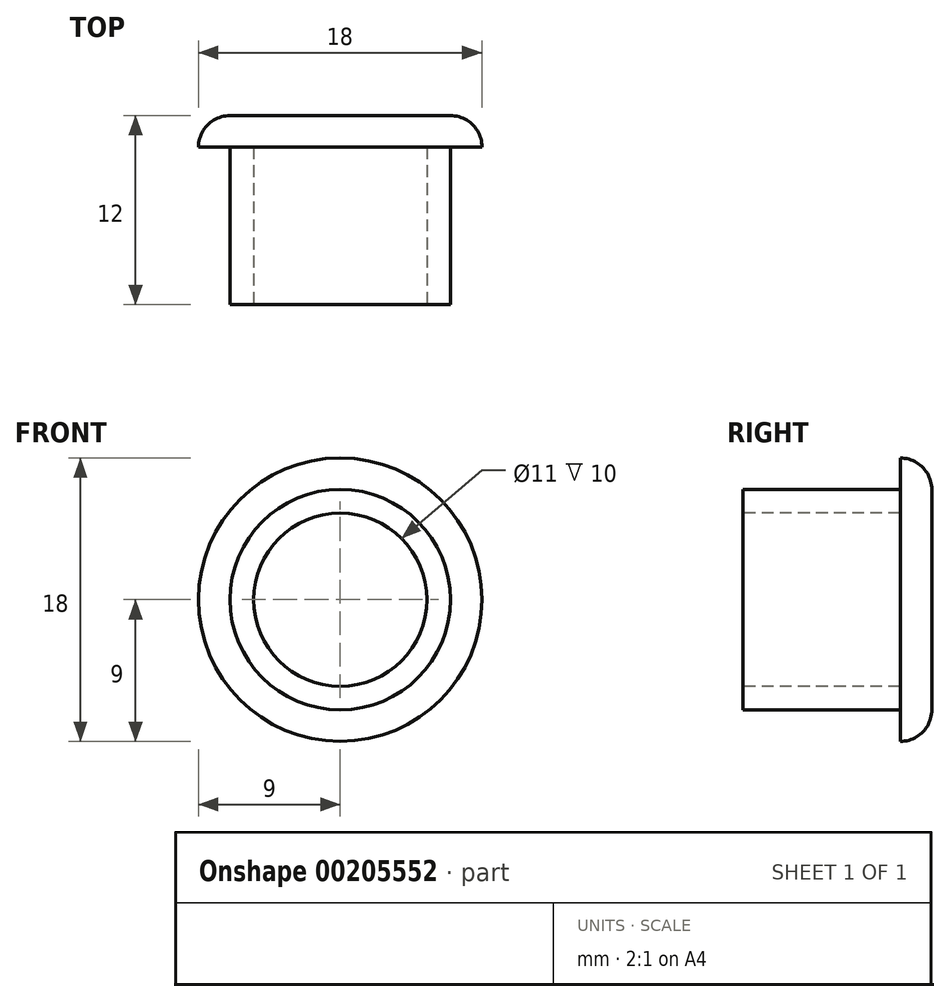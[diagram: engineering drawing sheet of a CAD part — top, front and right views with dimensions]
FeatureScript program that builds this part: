
annotation { "Feature Type Name" : "Feature", "Feature Type Description" : "" }
export const myFeature = defineFeature(function(context is Context, id is Id, definition is map)
    precondition{}
    {
        {
            var Q0;
            Q0=qCreatedBy(makeId("Front.planeOp"),FACE);
            var sketch = newSketch(context, id + "F0", { "sketchPlane" : qUnion([Q0])});
            skCircle(sketch, "E0", {"center": v(0, 0) * mm, "radius": 9 * mm});
            skSolve(sketch);
        }
        {
            var Q0;
            Q0=qSketchRegion(id+"F0",true);
            extrude(context, id + "F1", {"entities" : qUnion([Q0]), "depth" : 12 * mm});
        }
        {
            var Q0;
            Q0=makeQuery(id+"F1.opExtrude","CAP_FACE",FACE,{"disambiguationData":[OSD([sQuery(id+"F0.wireOp",EDGE,"E0")])],"isStart":false});
            var sketch = newSketch(context, id + "F2", { "sketchPlane" : qUnion([Q0])});
            skCircle(sketch, "E1", {"center": v(0, 0) * mm, "radius": 7 * mm});
            skSolve(sketch);
        }
        {
            var Q0;
            Q0=makeQuery(id+"F2.imprint","IMPRINT",FACE,{"disambiguationData":[TD([[makeQuery(id+"F2.imprint","IMPRINT",EDGE,{"derivedFrom":sQuery(id+"F2.wireOp",EDGE,"E1")}),-1.0]])]});
            extrude(context, id + "F3", {"entities" : qUnion([Q0]), "operationType" : NewBodyOperationType.REMOVE, "oppositeDirection" : true, "depth" : 10 * mm});
        }
        {
            var Q0;
            Q0=makeQuery(id+"F1.opExtrude","CAP_FACE",FACE,{"disambiguationData":[OSD([sQuery(id+"F0.wireOp",EDGE,"E0")])],"isStart":false});
            var sketch = newSketch(context, id + "F4", { "sketchPlane" : qUnion([Q0])});
            skCircle(sketch, "E2", {"center": v(0, 0) * mm, "radius": 5.5 * mm});
            skSolve(sketch);
        }
        {
            var Q0;
            Q0=qSketchRegion(id+"F4",true);
            extrude(context, id + "F5", {"entities" : qUnion([Q0]), "operationType" : NewBodyOperationType.REMOVE, "oppositeDirection" : true, "depth" : 10 * mm});
        }
        {
            var Q0;
            Q0=makeQuery(id+"F1.opExtrude","CAP_FACE",FACE,{"disambiguationData":[OSD([sQuery(id+"F0.wireOp",EDGE,"E0")])],"isStart":true});
            fillet(context, id + "F6", {"entities" : qUnion([Q0]), "radius" : 2 * mm, "tangentPropagation" : true, "allowEdgeOverflow" : false});
        }
    });
